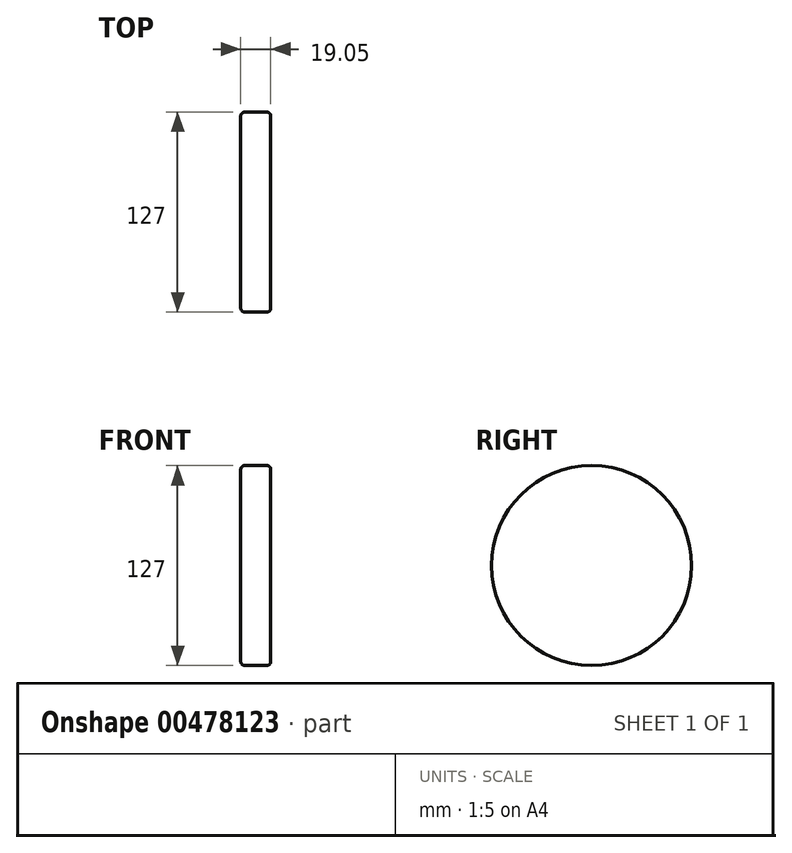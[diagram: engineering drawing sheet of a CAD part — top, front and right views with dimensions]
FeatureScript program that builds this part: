
annotation { "Feature Type Name" : "Feature", "Feature Type Description" : "" }
export const myFeature = defineFeature(function(context is Context, id is Id, definition is map)
    precondition{}
    {
        {
            var Q0;
            Q0=qCreatedBy(makeId("Right.planeOp"),FACE);
            var sketch = newSketch(context, id + "F0", { "sketchPlane" : qUnion([Q0])});
            skCircle(sketch, "E0", {"center": v(0, 0) * mm, "radius": 63.5 * mm});
            skSolve(sketch);
        }
        {
            var Q0;
            Q0=makeQuery(id+"F0.imprint","IMPRINT",FACE,{"disambiguationData":[TD([[makeQuery(id+"F0.imprint","IMPRINT",EDGE,{"derivedFrom":sQuery(id+"F0.wireOp",EDGE,"E0")}),1.0]])]});
            extrude(context, id + "F1", {"entities" : qUnion([Q0]), "depth" : 19.05 * mm, "offsetDistance" : 25.4 * mm});
        }
        {
            var Q0;
            Q0=makeQuery(id+"F1.opExtrude","CAP_EDGE",EDGE,{"disambiguationData":[OSD([sQuery(id+"F0.wireOp",EDGE,"E0")])],"isStart":false});
            fillet(context, id + "F2", {"entities" : qUnion([Q0]), "radius" : 2.54 * mm, "tangentPropagation" : true, "allowEdgeOverflow" : false});
        }
        {
            var Q0;
            Q0=makeQuery(id+"F1.opExtrude","CAP_EDGE",EDGE,{"disambiguationData":[OSD([sQuery(id+"F0.wireOp",EDGE,"E0")])],"isStart":true});
            fillet(context, id + "F3", {"entities" : qUnion([Q0]), "radius" : 2.54 * mm, "tangentPropagation" : true, "allowEdgeOverflow" : false});
        }
    });
